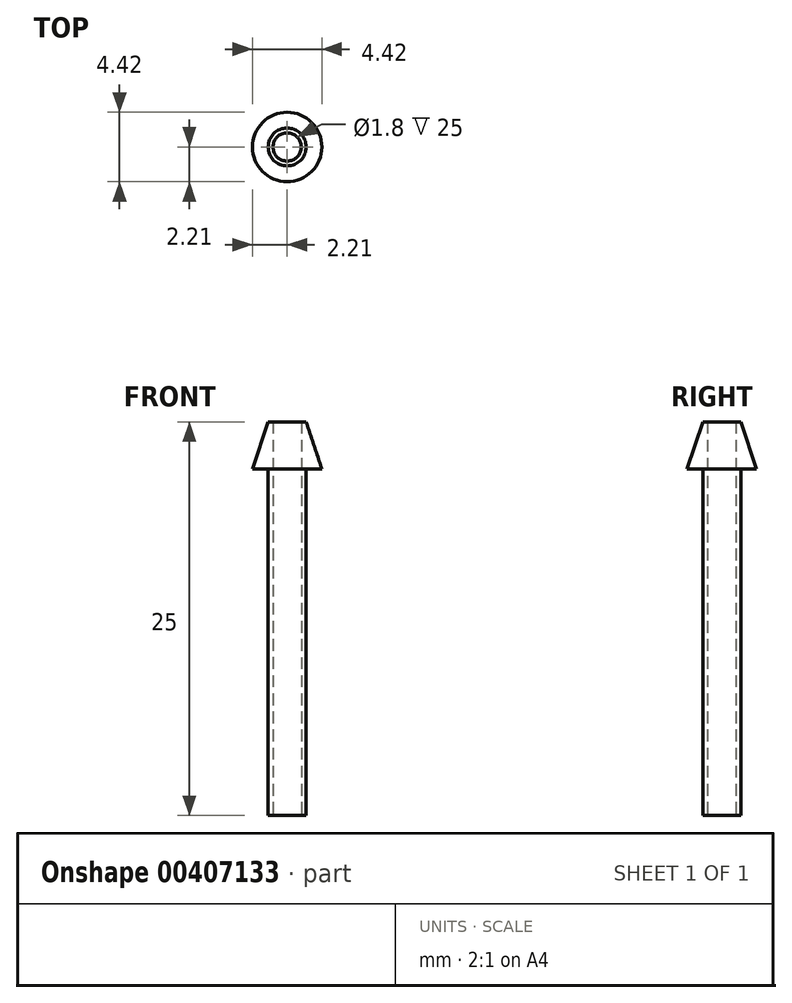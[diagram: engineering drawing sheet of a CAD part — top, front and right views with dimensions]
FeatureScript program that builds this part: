
annotation { "Feature Type Name" : "Feature", "Feature Type Description" : "" }
export const myFeature = defineFeature(function(context is Context, id is Id, definition is map)
    precondition{}
    {
        {
            var Q0;
            Q0=qCreatedBy(makeId("Top.planeOp"),FACE);
            var sketch = newSketch(context, id + "F0", { "sketchPlane" : qUnion([Q0])});
            skCircle(sketch, "E0", {"center": v(0, 0) * mm, "radius": 1.2 * mm});
            skCircle(sketch, "E1", {"center": v(0, 0) * mm, "radius": 0.9 * mm});
            skSolve(sketch);
        }
        {
            var Q0;
            Q0=qSketchRegion(id+"F0",true);
            extrude(context, id + "F1", {"entities" : qUnion([Q0]), "depth" : 25 * mm});
        }
        {
            var Q0;
            Q0=qCreatedBy(makeId("Front.planeOp"),FACE);
            var sketch = newSketch(context, id + "F2", { "sketchPlane" : qUnion([Q0])});
            skLineSegment(sketch, "E2", {"start": v(1.2, 25) * mm, "end": v(1.2, 11.9) * mm, "construction": true});
            skLineSegment(sketch, "E3.0", {"start": v(-1.2, 25) * mm, "end": v(1.2, 25) * mm, "construction": true});
            skLineSegment(sketch, "E4", {"start": v(1.2, 25) * mm, "end": v(2.2, 22) * mm});
            skLineSegment(sketch, "E5", {"start": v(2.2, 22) * mm, "end": v(1.2, 22) * mm});
            skLineSegment(sketch, "E6", {"start": v(1.2, 22) * mm, "end": v(1.2, 25) * mm});
            skLineSegment(sketch, "E7", {"start": v(0, 25) * mm, "end": v(0, 0) * mm, "construction": true});
            skSolve(sketch);
        }
        {
            var Q0;
            Q0=qSketchRegion(id+"F2",true);
            var Q1;
            Q1=sQuery(id+"F2.wireOp",EDGE,"E7");
            revolve(context, id + "F3", {"operationType" : NewBodyOperationType.ADD, "entities" : qUnion([Q0]), "axis" : qUnion([Q1]), "revolveType" : RevolveType.FULL});
        }
    });
